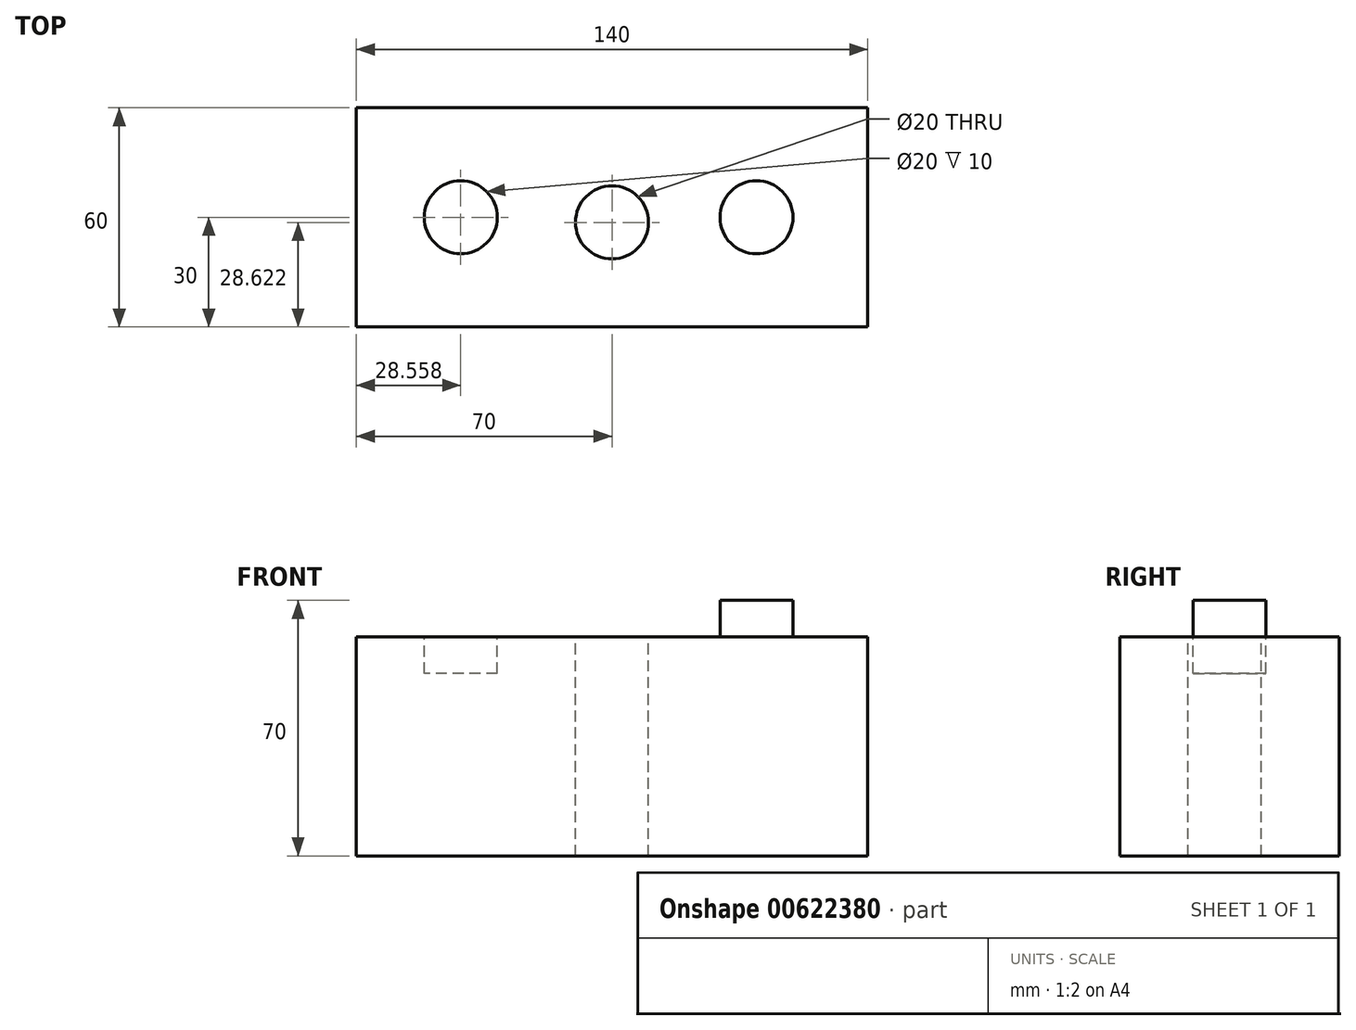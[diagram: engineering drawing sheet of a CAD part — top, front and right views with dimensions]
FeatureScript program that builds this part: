
annotation { "Feature Type Name" : "Feature", "Feature Type Description" : "" }
export const myFeature = defineFeature(function(context is Context, id is Id, definition is map)
    precondition{}
    {
        {
            var Q0;
            Q0=qCreatedBy(makeId("Top.planeOp"),FACE);
            var sketch = newSketch(context, id + "F0", { "sketchPlane" : qUnion([Q0])});
            skLineSegment(sketch, "E0.bottom", {"start": v(-70, -30) * mm, "end": v(70, -30) * mm});
            skLineSegment(sketch, "E0.top", {"start": v(-70, 30) * mm, "end": v(70, 30) * mm});
            skLineSegment(sketch, "E0.left", {"start": v(-70, -30) * mm, "end": v(-70, 30) * mm});
            skLineSegment(sketch, "E0.right", {"start": v(70, -30) * mm, "end": v(70, 30) * mm});
            skPoint(sketch, "E0.middle", {"position": v(0, 0) * mm});
            skSolve(sketch);
        }
        {
            var Q0;
            Q0 = qSketchRegion(id + "F0", true);
            extrude(context, id + "F1", {"entities" : qUnion([Q0]), "depth" : 60 * mm, "offsetDistance" : 25 * mm});
        }
        {
            var Q0;
            Q0=makeQuery(id+"F1.opExtrude","CAP_FACE",FACE,{"disambiguationData":[OSD([sQuery(id+"F0.wireOp",EDGE,"E0.bottom"),sQuery(id+"F0.wireOp",EDGE,"E0.top"),sQuery(id+"F0.wireOp",EDGE,"E0.left"),sQuery(id+"F0.wireOp",EDGE,"E0.right")])],"isStart":false});
            var sketch = newSketch(context, id + "F2", { "sketchPlane" : qUnion([Q0])});
            skCircle(sketch, "E1", {"center": v(0, -1.38) * mm, "radius": 10 * mm});
            skSolve(sketch);
        }
        {
            var Q0;
            Q0 = qSketchRegion(id + "F2", true);
            extrude(context, id + "F3", {"entities" : qUnion([Q0]), "operationType" : NewBodyOperationType.REMOVE, "oppositeDirection" : true, "depth" : 106.3 * mm, "offsetDistance" : 25 * mm});
        }
        {
            var Q0;
            Q0=makeQuery(id+"F1.opExtrude","CAP_FACE",FACE,{"disambiguationData":[OSD([sQuery(id+"F0.wireOp",EDGE,"E0.bottom"),sQuery(id+"F0.wireOp",EDGE,"E0.top"),sQuery(id+"F0.wireOp",EDGE,"E0.left"),sQuery(id+"F0.wireOp",EDGE,"E0.right")])],"isStart":false});
            var sketch = newSketch(context, id + "F4", { "sketchPlane" : qUnion([Q0])});
            skLineSegment(sketch, "E2", {"start": v(-29.9, 0) * mm, "end": v(-9.9, 0) * mm});
            skCircle(sketch, "E3", {"center": v(-41.44, 0) * mm, "radius": 10 * mm});
            skSolve(sketch);
        }
        {
            var Q0;
            Q0 = qSketchRegion(id + "F4", true);
            extrude(context, id + "F5", {"entities" : qUnion([Q0]), "operationType" : NewBodyOperationType.REMOVE, "oppositeDirection" : true, "depth" : 10 * mm, "offsetDistance" : 25 * mm});
        }
        {
            var Q0;
            Q0=makeQuery(id+"F1.opExtrude","CAP_FACE",FACE,{"disambiguationData":[OSD([sQuery(id+"F0.wireOp",EDGE,"E0.bottom"),sQuery(id+"F0.wireOp",EDGE,"E0.top"),sQuery(id+"F0.wireOp",EDGE,"E0.left"),sQuery(id+"F0.wireOp",EDGE,"E0.right")])],"isStart":false});
            var sketch = newSketch(context, id + "F6", { "sketchPlane" : qUnion([Q0])});
            skLineSegment(sketch, "E4", {"start": v(9.9, 0) * mm, "end": v(29.9, 0) * mm});
            skCircle(sketch, "E5", {"center": v(39.56, 0) * mm, "radius": 10 * mm});
            skSolve(sketch);
        }
        {
            var Q0;
            Q0 = qSketchRegion(id + "F6", true);
            extrude(context, id + "F7", {"entities" : qUnion([Q0]), "operationType" : NewBodyOperationType.ADD, "depth" : 10 * mm, "offsetDistance" : 25 * mm});
        }
    });
